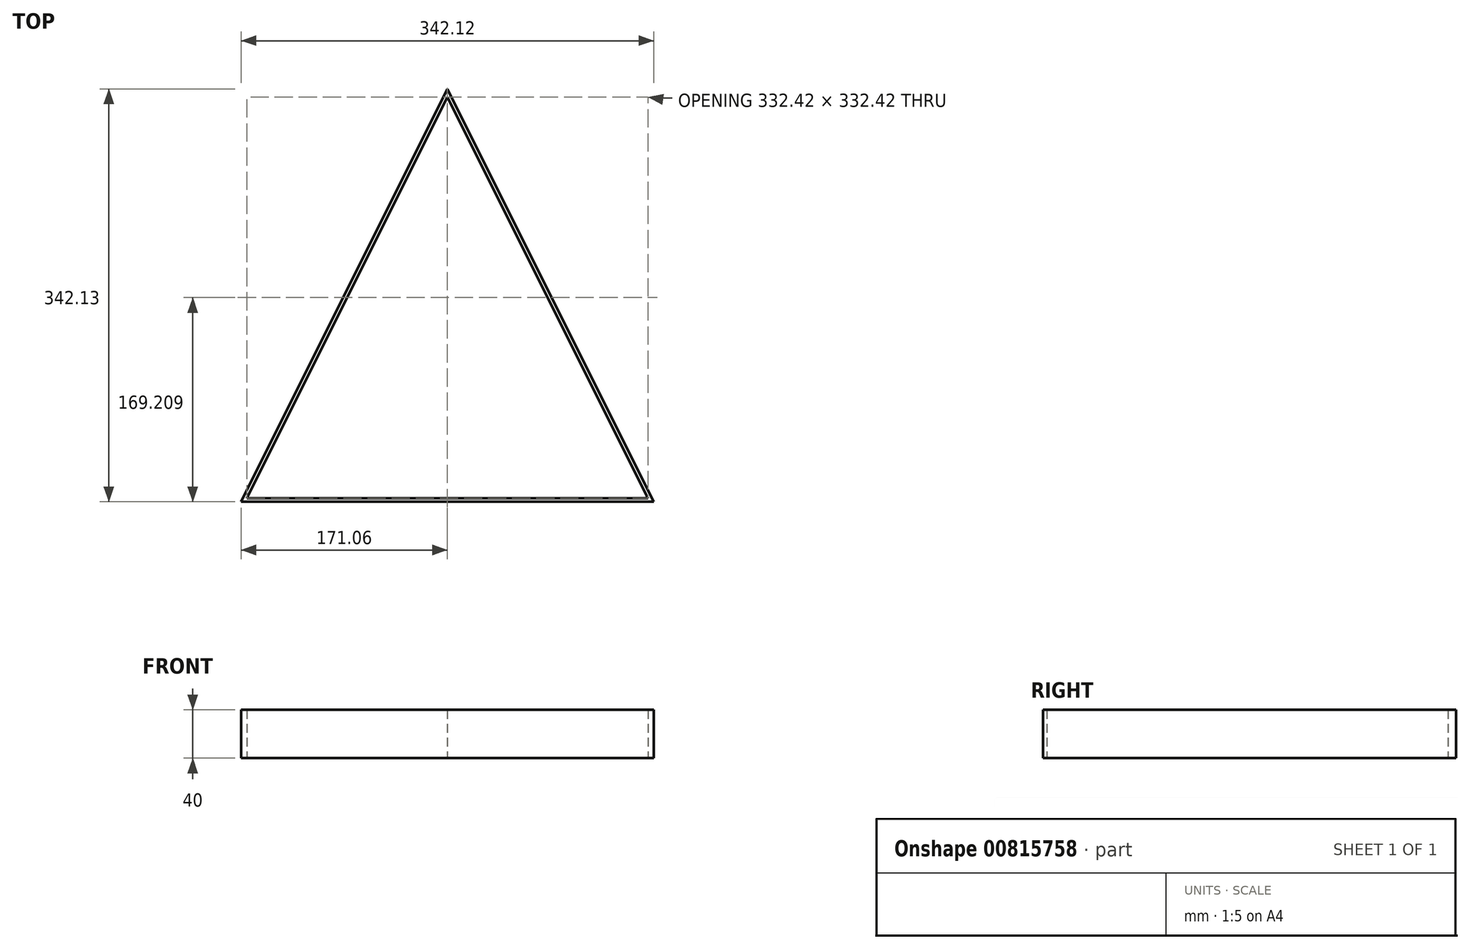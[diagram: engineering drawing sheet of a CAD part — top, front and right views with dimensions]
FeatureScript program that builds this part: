
annotation { "Feature Type Name" : "Feature", "Feature Type Description" : "" }
export const myFeature = defineFeature(function(context is Context, id is Id, definition is map)
    precondition{}
    {
        {
            var Q0;
            Q0=qCreatedBy(makeId("Top.planeOp"),FACE);
            var sketch = newSketch(context, id + "F0", { "sketchPlane" : qUnion([Q0])});
            skLineSegment(sketch, "E0", {"start": v(0, 0) * mm, "end": v(0, 342.13) * mm, "construction": true});
            skLineSegment(sketch, "E1.bottom", {"start": v(171.06, 0) * mm, "end": v(-171.06, 0) * mm, "construction": true});
            skLineSegment(sketch, "E1.top", {"start": v(171.06, 0) * mm, "end": v(-171.06, 0) * mm});
            skLineSegment(sketch, "E1.left", {"start": v(171.06, 0) * mm, "end": v(171.06, 0) * mm});
            skLineSegment(sketch, "E1.right", {"start": v(-171.06, 0) * mm, "end": v(-171.06, 0) * mm});
            skPoint(sketch, "E1.middle", {"position": v(0, 0) * mm});
            skLineSegment(sketch, "E2", {"start": v(0, 342.13) * mm, "end": v(171.06, 0) * mm});
            skLineSegment(sketch, "E3", {"start": v(-171.06, 0) * mm, "end": v(0, 342.13) * mm});
            skLineSegment(sketch, "E4", {"start": v(0, 335.42) * mm, "end": v(166.2, 3) * mm});
            skLineSegment(sketch, "E5", {"start": v(166.2, 3) * mm, "end": v(-166.2, 3) * mm});
            skLineSegment(sketch, "E6", {"start": v(-166.2, 3) * mm, "end": v(0, 335.42) * mm});
            skSolve(sketch);
        }
        {
            var Q0;
            Q0 = qSketchRegion(id + "F0", true);
            extrude(context, id + "F1", {"entities" : qUnion([Q0]), "depth" : 40 * mm, "offsetDistance" : 25 * mm});
        }
    });
